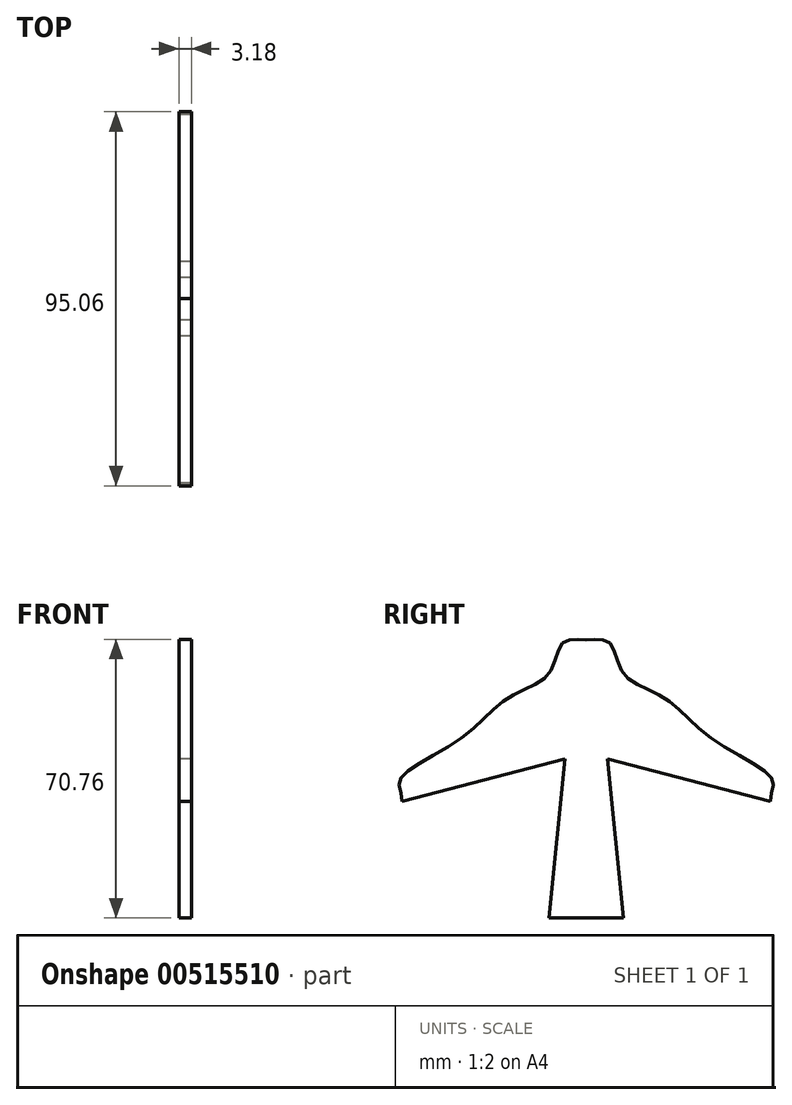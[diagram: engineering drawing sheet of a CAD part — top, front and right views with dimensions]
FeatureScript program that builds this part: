
annotation { "Feature Type Name" : "Feature", "Feature Type Description" : "" }
export const myFeature = defineFeature(function(context is Context, id is Id, definition is map)
    precondition{}
    {
        {
            var Q0;
            Q0=qCreatedBy(makeId("Right.planeOp"),FACE);
            var sketch = newSketch(context, id + "F0", { "sketchPlane" : qUnion([Q0])});
            skLineSegment(sketch, "E0.bottom", {"start": v(0, -29.54) * mm, "end": v(9.41, -29.54) * mm});
            skLineSegment(sketch, "E0.left", {"start": v(0, -29.54) * mm, "end": v(0, -29.54) * mm});
            skLineSegment(sketch, "E0.right", {"start": v(9.41, -29.54) * mm, "end": v(5.42, 10.88) * mm});
            skLineSegment(sketch, "E1", {"start": v(5.42, 10.88) * mm, "end": v(46.76, 0) * mm});
            skPoint(sketch, "E2.5.internal.orphan", {"position": v(0, 33.42) * mm});
            skPoint(sketch, "E2.6.internal.orphan", {"position": v(0, 33.42) * mm});
            skFitSpline(sketch, "E3", {"points": [v(46.76, 0) * mm, v(47.3, 5.62) * mm, v(32.27, 15.7) * mm, v(19.51, 26.59) * mm, v(9.35, 32.63) * mm, v(5.79, 40.49) * mm, v(0, 41.12) * mm], "startDerivative": vector(-0.99, 57.25) * mm, "endDerivative": vector(-43.63, 0.91) * mm});
            skLineSegment(sketch, "E4", {"start": v(0, 41.12) * mm, "end": v(0, -29.54) * mm});
            skFitSpline(sketch, "E5.MirrorCS", {"points": [v(-46.76, 0) * mm, v(-47.3, 5.62) * mm, v(-32.27, 15.7) * mm, v(-19.51, 26.59) * mm, v(-9.35, 32.63) * mm, v(-5.79, 40.49) * mm, v(0, 41.12) * mm], "startDerivative": vector(0.99, 57.25) * mm, "endDerivative": vector(43.63, 0.91) * mm});
            skLineSegment(sketch, "E6.MirrorCS", {"start": v(-5.42, 10.88) * mm, "end": v(-46.76, 0) * mm});
            skLineSegment(sketch, "E7.MirrorCS", {"start": v(-9.41, -29.54) * mm, "end": v(-5.42, 10.88) * mm});
            skLineSegment(sketch, "E8.MirrorCS", {"start": v(0, -29.54) * mm, "end": v(-9.41, -29.54) * mm});
            skSolve(sketch);
        }
        {
            var Q0;
            Q0=makeQuery(id+"F0.imprint","IMPRINT",FACE,{"disambiguationData":[TD([[makeQuery(id+"F0.imprint","IMPRINT",EDGE,{"derivedFrom":sQuery(id+"F0.wireOp",EDGE,"E4")}),-1.0]])]});
            var Q1;
            Q1=makeQuery(id+"F0.imprint","IMPRINT",FACE,{"disambiguationData":[TD([[makeQuery(id+"F0.imprint","IMPRINT",EDGE,{"derivedFrom":sQuery(id+"F0.wireOp",EDGE,"E0.bottom")}),1.0]])]});
            extrude(context, id + "F1", {"entities" : qUnion([Q0, Q1]), "depth" : 3.17 * mm, "offsetDistance" : 25.4 * mm});
        }
    });
